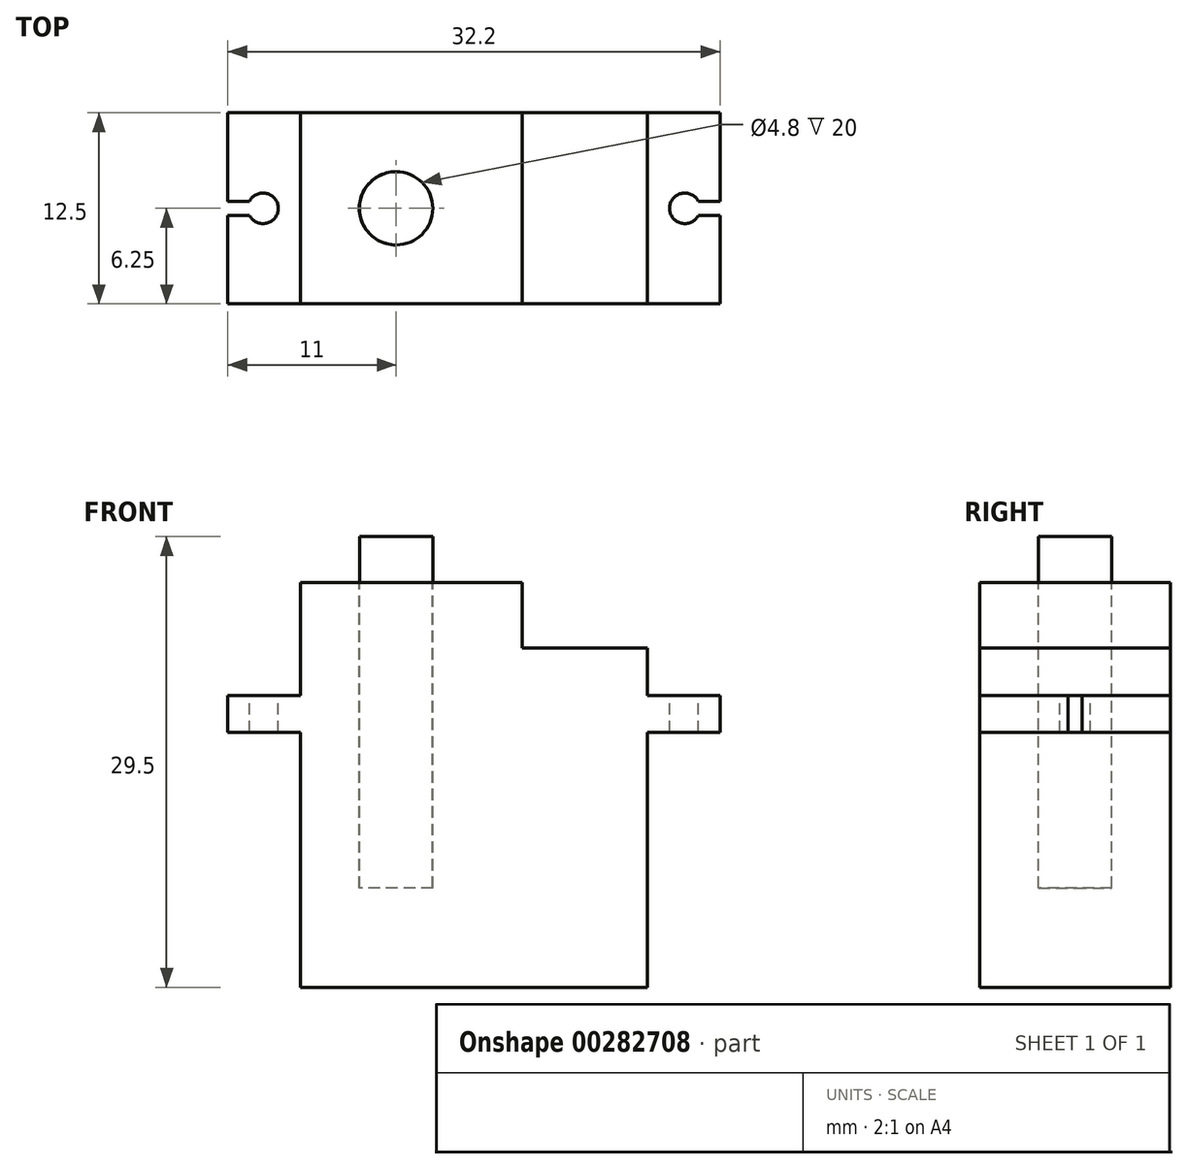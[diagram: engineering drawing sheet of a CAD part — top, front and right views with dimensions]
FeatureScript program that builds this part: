
annotation { "Feature Type Name" : "Feature", "Feature Type Description" : "" }
export const myFeature = defineFeature(function(context is Context, id is Id, definition is map)
    precondition{}
    {
        {
            var Q0;
            Q0=qCreatedBy(makeId("Top.planeOp"),FACE);
            var sketch = newSketch(context, id + "F0", { "sketchPlane" : qUnion([Q0])});
            skLineSegment(sketch, "E0.bottom", {"start": v(11.35, 6.25) * mm, "end": v(-11.35, 6.25) * mm});
            skLineSegment(sketch, "E0.top", {"start": v(11.35, -6.25) * mm, "end": v(-11.35, -6.25) * mm});
            skLineSegment(sketch, "E0.left", {"start": v(11.35, 6.25) * mm, "end": v(11.35, -6.25) * mm});
            skLineSegment(sketch, "E0.right", {"start": v(-11.35, 6.25) * mm, "end": v(-11.35, -6.25) * mm});
            skPoint(sketch, "E0.middle", {"position": v(0, 0) * mm});
            skSolve(sketch);
        }
        {
            var Q0;
            Q0=qSketchRegion(id+"F0",true);
            extrude(context, id + "F1", {"entities" : qUnion([Q0]), "depth" : 16.7 * mm});
        }
        {
            var Q0;
            Q0=makeQuery(id+"F1.opExtrude","CAP_FACE",FACE,{"disambiguationData":[OSD([sQuery(id+"F0.wireOp",EDGE,"E0.bottom"),sQuery(id+"F0.wireOp",EDGE,"E0.top"),sQuery(id+"F0.wireOp",EDGE,"E0.left"),sQuery(id+"F0.wireOp",EDGE,"E0.right")])],"isStart":false});
            var sketch = newSketch(context, id + "F2", { "sketchPlane" : qUnion([Q0])});
            skLineSegment(sketch, "E1.bottom", {"start": v(16.1, -6.25) * mm, "end": v(-16.1, -6.25) * mm});
            skLineSegment(sketch, "E1.top", {"start": v(16.1, 6.25) * mm, "end": v(-16.1, 6.25) * mm});
            skLineSegment(sketch, "E1.left", {"start": v(16.1, -6.25) * mm, "end": v(16.1, 6.25) * mm});
            skLineSegment(sketch, "E1.right", {"start": v(-16.1, -6.25) * mm, "end": v(-16.1, 6.25) * mm});
            skPoint(sketch, "E1.middle", {"position": v(0, 0) * mm});
            skSolve(sketch);
        }
        {
            var Q0;
            Q0=qSketchRegion(id+"F2",true);
            extrude(context, id + "F3", {"entities" : qUnion([Q0]), "operationType" : NewBodyOperationType.ADD, "depth" : 2.4 * mm});
        }
        {
            var Q0;
            Q0=makeQuery(id+"F3.opExtrude","CAP_FACE",FACE,{"disambiguationData":[OSD([sQuery(id+"F2.wireOp",EDGE,"E1.bottom"),sQuery(id+"F2.wireOp",EDGE,"E1.top"),sQuery(id+"F2.wireOp",EDGE,"E1.left"),sQuery(id+"F2.wireOp",EDGE,"E1.right")])],"isStart":false});
            var sketch = newSketch(context, id + "F4", { "sketchPlane" : qUnion([Q0])});
            skLineSegment(sketch, "E2", {"start": v(-16.1, 0) * mm, "end": v(16.1, 0) * mm, "construction": true});
            skCircle(sketch, "E3", {"center": v(0, 0) * mm, "radius": 13.8 * mm, "construction": true});
            skCircle(sketch, "E4", {"center": v(-13.8, 0) * mm, "radius": 1 * mm});
            skLineSegment(sketch, "E5.bottom", {"start": v(-16.1, 0.46) * mm, "end": v(-13.5, 0.46) * mm});
            skLineSegment(sketch, "E5.top", {"start": v(-16.1, -0.46) * mm, "end": v(-13.5, -0.46) * mm});
            skLineSegment(sketch, "E5.left", {"start": v(-16.1, 0.46) * mm, "end": v(-16.1, -0.46) * mm});
            skLineSegment(sketch, "E5.right", {"start": v(-13.5, 0.46) * mm, "end": v(-13.5, -0.46) * mm});
            skPoint(sketch, "E5.middle", {"position": v(-14.8, 0) * mm});
            skLineSegment(sketch, "E6.MirrorCS", {"start": v(13.5, 0.46) * mm, "end": v(13.5, -0.46) * mm});
            skLineSegment(sketch, "E7.MirrorCS", {"start": v(16.1, 0.46) * mm, "end": v(16.1, -0.46) * mm});
            skLineSegment(sketch, "E8.MirrorCS", {"start": v(16.1, 0.46) * mm, "end": v(13.5, 0.46) * mm});
            skLineSegment(sketch, "E9.MirrorCS", {"start": v(16.1, -0.46) * mm, "end": v(13.5, -0.46) * mm});
            skCircle(sketch, "E10.MirrorC", {"center": v(13.8, 0) * mm, "radius": 1 * mm});
            skPoint(sketch, "E11.MirrorP", {"position": v(14.8, 0) * mm});
            skSolve(sketch);
        }
        {
            var Q0;
            Q0=qSketchRegion(id+"F4",true);
            extrude(context, id + "F5", {"entities" : qUnion([Q0]), "operationType" : NewBodyOperationType.REMOVE, "endBound" : BoundingType.THROUGH_ALL, "oppositeDirection" : true, "depth" : 25 * mm});
        }
        {
            var Q0;
            Q0=makeQuery(id+"F1.opExtrude","CAP_FACE",FACE,{"disambiguationData":[OSD([sQuery(id+"F0.wireOp",EDGE,"E0.bottom"),sQuery(id+"F0.wireOp",EDGE,"E0.top"),sQuery(id+"F0.wireOp",EDGE,"E0.left"),sQuery(id+"F0.wireOp",EDGE,"E0.right")])],"isStart":true});
            extrude(context, id + "F6", {"entities" : qUnion([Q0]), "operationType" : NewBodyOperationType.ADD, "oppositeDirection" : true, "depth" : 22.2 * mm});
        }
        {
            var Q0;
            Q0=makeQuery(id+"F6.opExtrude","CAP_FACE",FACE,{"disambiguationData":[OSD([sQuery(id+"F0.wireOp",EDGE,"E0.bottom"),sQuery(id+"F0.wireOp",EDGE,"E0.top"),sQuery(id+"F0.wireOp",EDGE,"E0.left"),sQuery(id+"F0.wireOp",EDGE,"E0.right")])],"isStart":false});
            var sketch = newSketch(context, id + "F7", { "sketchPlane" : qUnion([Q0])});
            skLineSegment(sketch, "E12.bottom", {"start": v(-11.35, 6.25) * mm, "end": v(3.15, 6.25) * mm});
            skLineSegment(sketch, "E12.top", {"start": v(-11.35, -6.25) * mm, "end": v(3.15, -6.25) * mm});
            skLineSegment(sketch, "E12.left", {"start": v(-11.35, 6.25) * mm, "end": v(-11.35, -6.25) * mm});
            skLineSegment(sketch, "E12.right", {"start": v(3.15, 6.25) * mm, "end": v(3.15, -6.25) * mm});
            skSolve(sketch);
        }
        {
            var Q0;
            Q0=qSketchRegion(id+"F7",true);
            extrude(context, id + "F8", {"entities" : qUnion([Q0]), "operationType" : NewBodyOperationType.ADD, "depth" : 4.3 * mm});
        }
        {
            var Q0;
            Q0=makeQuery(id+"F8.opExtrude","CAP_FACE",FACE,{"disambiguationData":[OSD([sQuery(id+"F7.wireOp",EDGE,"E12.bottom"),sQuery(id+"F7.wireOp",EDGE,"E12.top"),sQuery(id+"F7.wireOp",EDGE,"E12.left"),sQuery(id+"F7.wireOp",EDGE,"E12.right")])],"isStart":false});
            var sketch = newSketch(context, id + "F9", { "sketchPlane" : qUnion([Q0])});
            skCircle(sketch, "E13", {"center": v(-11.35, 0) * mm, "radius": 6.25 * mm, "construction": true});
            skCircle(sketch, "E14", {"center": v(-5.1, 0) * mm, "radius": 2.4 * mm});
            skSolve(sketch);
        }
        {
            var Q0;
            Q0=makeQuery(id+"F1.opExtrude","SWEPT_BODY",BODY,{"disambiguationData":[OSD([sQuery(id+"F0.wireOp",EDGE,"E0.bottom"),sQuery(id+"F0.wireOp",EDGE,"E0.top"),sQuery(id+"F0.wireOp",EDGE,"E0.left"),sQuery(id+"F0.wireOp",EDGE,"E0.right")])]});
            transform(context, id + "F10", {"entities" : qUnion([Q0]), "transformType" : TransformType.TRANSLATION_3D, "dx" : 0 * mm, "dy" : 0 * mm, "dz" : 0 * mm, "makeCopy" : true});
        }
        {
            var Q0;
            Q0=makeQuery(id+"F10.opPattern","COPY",BODY,{"derivedFrom":makeQuery(id+"F1.opExtrude","SWEPT_BODY",BODY,{"disambiguationData":[OSD([sQuery(id+"F0.wireOp",EDGE,"E0.bottom"),sQuery(id+"F0.wireOp",EDGE,"E0.top"),sQuery(id+"F0.wireOp",EDGE,"E0.left"),sQuery(id+"F0.wireOp",EDGE,"E0.right")])]}),"instanceName":"1"});
            deleteBodies(context, id + "F11", {"entities" : qUnion([Q0])});
        }
        {
            var Q0;
            Q0=makeQuery(id+"F8.opExtrude","CAP_FACE",FACE,{"disambiguationData":[OSD([sQuery(id+"F7.wireOp",EDGE,"E12.bottom"),sQuery(id+"F7.wireOp",EDGE,"E12.top"),sQuery(id+"F7.wireOp",EDGE,"E12.left"),sQuery(id+"F7.wireOp",EDGE,"E12.right")])],"isStart":false});
            var sketch = newSketch(context, id + "F12", { "sketchPlane" : qUnion([Q0])});
            skCircle(sketch, "E15", {"center": v(-5.1, 0) * mm, "radius": 2.4 * mm});
            skSolve(sketch);
        }
        {
            var Q0;
            Q0=qSketchRegion(id+"F12",true);
            extrude(context, id + "F13", {"entities" : qUnion([Q0]), "operationType" : NewBodyOperationType.REMOVE, "oppositeDirection" : true, "depth" : 20 * mm});
        }
        {
            var Q0;
            Q0=makeQuery(id+"F9.imprint","IMPRINT",FACE,{"disambiguationData":[TD([[makeQuery(id+"F9.imprint","IMPRINT",EDGE,{"derivedFrom":sQuery(id+"F9.wireOp",EDGE,"E14")}),-1.0]])]});
            var sketch = newSketch(context, id + "F14", { "sketchPlane" : qUnion([Q0])});
            skCircle(sketch, "E16", {"center": v(-5.1, 0) * mm, "radius": 2.4 * mm});
            skSolve(sketch);
        }
        {
            var Q0;
            Q0=qSketchRegion(id+"F14",true);
            extrude(context, id + "F15", {"entities" : qUnion([Q0]), "depth" : 3 * mm});
        }
        {
            var Q0;
            Q0=makeQuery(id+"F15.opExtrude","CAP_FACE",FACE,{"disambiguationData":[OSD([sQuery(id+"F14.wireOp",EDGE,"E16")])],"isStart":false});
            extrude(context, id + "F16", {"entities" : qUnion([Q0]), "oppositeDirection" : true, "depth" : 23 * mm});
        }
        {
            var Q0;
            Q0=makeQuery(id+"F15.opExtrude","SWEPT_BODY",BODY,{"disambiguationData":[OSD([sQuery(id+"F14.wireOp",EDGE,"E16")])]});
            deleteBodies(context, id + "F17", {"entities" : qUnion([Q0])});
        }
    });
